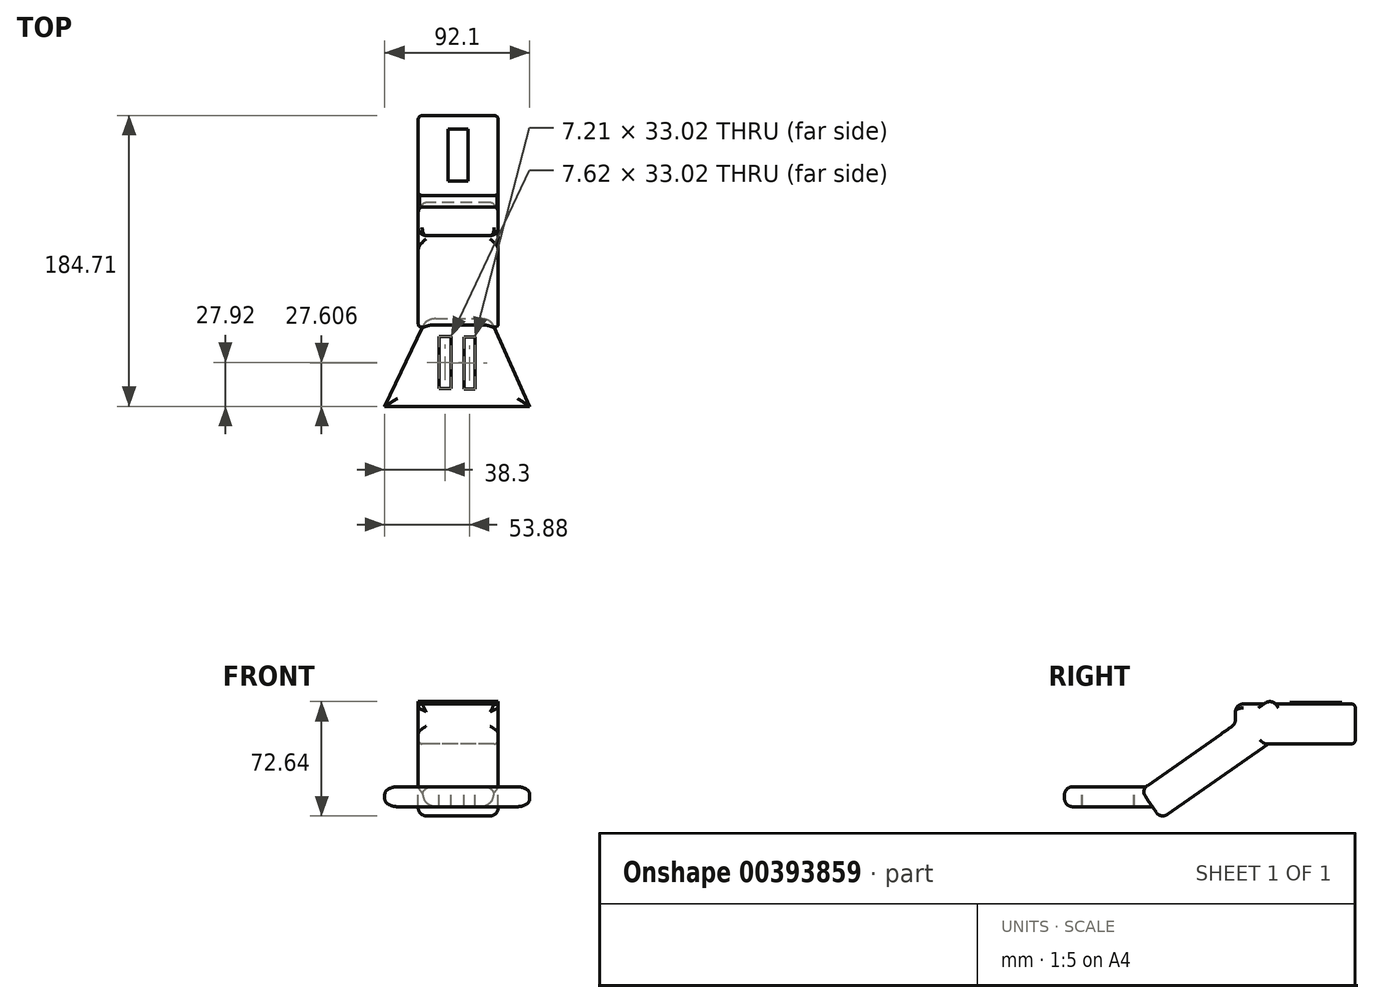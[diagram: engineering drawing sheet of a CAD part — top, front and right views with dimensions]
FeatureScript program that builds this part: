
annotation { "Feature Type Name" : "Feature", "Feature Type Description" : "" }
export const myFeature = defineFeature(function(context is Context, id is Id, definition is map)
    precondition{}
    {
        {
            var Q0;
            Q0=qCreatedBy(makeId("Front.planeOp"),FACE);
            var sketch = newSketch(context, id + "F0", { "sketchPlane" : qUnion([Q0])});
            skLineSegment(sketch, "E0.bottom", {"start": v(25.4, 12.7) * mm, "end": v(-25.4, 12.7) * mm});
            skLineSegment(sketch, "E0.top", {"start": v(25.4, -12.7) * mm, "end": v(-25.4, -12.7) * mm});
            skLineSegment(sketch, "E0.left", {"start": v(25.4, 12.7) * mm, "end": v(25.4, -12.7) * mm});
            skLineSegment(sketch, "E0.right", {"start": v(-25.4, 12.7) * mm, "end": v(-25.4, -12.7) * mm});
            skPoint(sketch, "E0.middle", {"position": v(0, 0) * mm});
            skSolve(sketch);
        }
        {
            var Q0;
            Q0=makeQuery(id+"F0.imprint","IMPRINT",FACE,{"disambiguationData":[TD([[makeQuery(id+"F0.imprint","IMPRINT",EDGE,{"derivedFrom":sQuery(id+"F0.wireOp",EDGE,"E0.bottom")}),1.0]])]});
            extrude(context, id + "F1", {"entities" : qUnion([Q0]), "oppositeDirection" : true, "depth" : 76.2 * mm});
        }
        {
            var Q0;
            Q0=makeQuery(id+"F1.opExtrude","SWEPT_EDGE",EDGE,{"disambiguationData":[OSD([sQuery(id+"F0.wireOp",EDGE,"E0.bottom"),sQuery(id+"F0.wireOp",EDGE,"E0.left")])]});
            var Q1;
            Q1=makeQuery(id+"F1.opExtrude","SWEPT_EDGE",EDGE,{"disambiguationData":[OSD([sQuery(id+"F0.wireOp",EDGE,"E0.bottom"),sQuery(id+"F0.wireOp",EDGE,"E0.right")])]});
            var Q2;
            Q2=makeQuery(id+"F1.opExtrude","SWEPT_EDGE",EDGE,{"disambiguationData":[OSD([sQuery(id+"F0.wireOp",EDGE,"E0.top"),sQuery(id+"F0.wireOp",EDGE,"E0.left")])]});
            var Q3;
            Q3=makeQuery(id+"F1.opExtrude","SWEPT_EDGE",EDGE,{"disambiguationData":[OSD([sQuery(id+"F0.wireOp",EDGE,"E0.top"),sQuery(id+"F0.wireOp",EDGE,"E0.right")])]});
            var Q4;
            Q4=makeQuery(id+"F1.opExtrude","CAP_EDGE",EDGE,{"disambiguationData":[OSD([sQuery(id+"F0.wireOp",EDGE,"E0.bottom")])],"isStart":false});
            var Q5;
            Q5=makeQuery(id+"F1.opExtrude","CAP_EDGE",EDGE,{"disambiguationData":[OSD([sQuery(id+"F0.wireOp",EDGE,"E0.right")])],"isStart":false});
            var Q6;
            Q6=makeQuery(id+"F1.opExtrude","CAP_EDGE",EDGE,{"disambiguationData":[OSD([sQuery(id+"F0.wireOp",EDGE,"E0.top")])],"isStart":false});
            var Q7;
            Q7=makeQuery(id+"F1.opExtrude","CAP_EDGE",EDGE,{"disambiguationData":[OSD([sQuery(id+"F0.wireOp",EDGE,"E0.left")])],"isStart":false});
            fillet(context, id + "F2", {"entities" : qUnion([Q0, Q1, Q2, Q3, Q4, Q5, Q6, Q7]), "radius" : 2.54 * mm, "tangentPropagation" : true, "allowEdgeOverflow" : false});
        }
        {
            var Q0;
            Q0=qCreatedBy(makeId("Front.planeOp"),FACE);
            cPlane(context, id + "F3", {"entities" : qUnion([Q0]), "cplaneType" : CPlaneType.OFFSET, "offset" : 50.8 * mm, "width" : 152.4 * mm, "height" : 152.4 * mm});
        }
        {
            var Q0;
            Q0=qCreatedBy(makeId("Top.planeOp"),FACE);
            var sketch = newSketch(context, id + "F4", { "sketchPlane" : qUnion([Q0])});
            skLineSegment(sketch, "E1", {"start": v(-76, 0) * mm, "end": v(75.54, 0) * mm, "construction": true});
            skSolve(sketch);
        }
        {
            var Q0;
            Q0=qCreatedBy(makeId("Top.planeOp"),FACE);
            var Q1;
            Q1=sQuery(id+"F4.wireOp",EDGE,"E1");
            cPlane(context, id + "F5", {"entities" : qUnion([Q0, Q1]), "cplaneType" : CPlaneType.LINE_ANGLE, "offset" : 25.4 * mm, "angle" : 35 * degree, "width" : 152.4 * mm, "height" : 152.4 * mm});
        }
        {
            var Q0;
            Q0=qCreatedBy(id+"F5.planeOp",FACE);
            var sketch = newSketch(context, id + "F6", { "sketchPlane" : qUnion([Q0])});
            skLineSegment(sketch, "E2.bottom", {"start": v(25.4, 73.45) * mm, "end": v(-25.4, 73.45) * mm});
            skLineSegment(sketch, "E2.top", {"start": v(25.4, -28.15) * mm, "end": v(-25.4, -28.15) * mm});
            skLineSegment(sketch, "E2.left", {"start": v(25.4, 73.45) * mm, "end": v(25.4, -28.15) * mm});
            skLineSegment(sketch, "E2.right", {"start": v(-25.4, 73.45) * mm, "end": v(-25.4, -28.15) * mm});
            skPoint(sketch, "E2.middle", {"position": v(0, 22.65) * mm});
            skSolve(sketch);
        }
        {
            var Q0;
            Q0=makeQuery(id+"F6.imprint","IMPRINT",FACE,{"disambiguationData":[TD([[makeQuery(id+"F6.imprint","IMPRINT",EDGE,{"derivedFrom":sQuery(id+"F6.wireOp",EDGE,"E2.bottom")}),1.0]])]});
            extrude(context, id + "F7", {"entities" : qUnion([Q0]), "operationType" : NewBodyOperationType.ADD, "depth" : 22.35 * mm});
        }
        {
            var Q0;
            Q0=makeQuery(id+"F7.opExtrude","CAP_EDGE",EDGE,{"disambiguationData":[OSD([sQuery(id+"F6.wireOp",EDGE,"E2.top")])],"isStart":true});
            var Q1;
            Q1=makeQuery(id+"F1.opExtrude","CAP_FACE",FACE,{"disambiguationData":[OSD([sQuery(id+"F0.wireOp",EDGE,"E0.bottom"),sQuery(id+"F0.wireOp",EDGE,"E0.top"),sQuery(id+"F0.wireOp",EDGE,"E0.left"),sQuery(id+"F0.wireOp",EDGE,"E0.right")])],"isStart":true});
            var Q2;
            Q2=makeQuery(id+"F7.opExtrude","CAP_EDGE",EDGE,{"disambiguationData":[OSD([sQuery(id+"F6.wireOp",EDGE,"E2.left")])],"isStart":false});
            var Q3;
            Q3=makeQuery(id+"F7.opExtrude","CAP_EDGE",EDGE,{"disambiguationData":[OSD([sQuery(id+"F6.wireOp",EDGE,"E2.right")])],"isStart":false});
            var Q4;
            Q4=makeQuery(id+"F7.opExtrude","CAP_EDGE",EDGE,{"disambiguationData":[OSD([sQuery(id+"F6.wireOp",EDGE,"E2.bottom")])],"isStart":false});
            var Q5;
            Q5=makeQuery(id+"F7.opExtrude","SWEPT_EDGE",EDGE,{"disambiguationData":[OSD([sQuery(id+"F6.wireOp",EDGE,"E2.bottom"),sQuery(id+"F6.wireOp",EDGE,"E2.left")])]});
            var Q6;
            Q6=makeQuery(id+"F7.opExtrude","CAP_EDGE",EDGE,{"disambiguationData":[OSD([sQuery(id+"F6.wireOp",EDGE,"E2.bottom")])],"isStart":true});
            var Q7;
            Q7=makeQuery(id+"F7.opExtrude","SWEPT_EDGE",EDGE,{"disambiguationData":[OSD([sQuery(id+"F6.wireOp",EDGE,"E2.bottom"),sQuery(id+"F6.wireOp",EDGE,"E2.right")])]});
            fillet(context, id + "F8", {"entities" : qUnion([Q0, Q1, Q2, Q3, Q4, Q5, Q6, Q7]), "radius" : 5.08 * mm, "tangentPropagation" : true, "allowEdgeOverflow" : false});
        }
        {
            var Q0;
            Q0=qCreatedBy(makeId("Top.planeOp"),FACE);
            cPlane(context, id + "F9", {"entities" : qUnion([Q0]), "cplaneType" : CPlaneType.OFFSET, "offset" : 52.58 * mm, "oppositeDirection" : true, "width" : 152.4 * mm, "height" : 152.4 * mm});
        }
        {
            var Q0;
            Q0=qCreatedBy(id+"F9.planeOp",FACE);
            var sketch = newSketch(context, id + "F10", { "sketchPlane" : qUnion([Q0])});
            skLineSegment(sketch, "E3", {"start": v(19.22, -50.68) * mm, "end": v(45.43, -108.51) * mm});
            skLineSegment(sketch, "E4", {"start": v(45.43, -108.51) * mm, "end": v(-46.67, -108.51) * mm});
            skLineSegment(sketch, "E5", {"start": v(-46.67, -108.51) * mm, "end": v(-19.27, -51.23) * mm});
            skLineSegment(sketch, "E6", {"start": v(-19.27, -51.23) * mm, "end": v(19.22, -50.68) * mm});
            skSolve(sketch);
        }
        {
            var Q0;
            Q0=makeQuery(id+"F10.imprint","IMPRINT",FACE,{"disambiguationData":[TD([[makeQuery(id+"F10.imprint","IMPRINT",EDGE,{"derivedFrom":sQuery(id+"F10.wireOp",EDGE,"E3")}),-1.0]])]});
            extrude(context, id + "F11", {"entities" : qUnion([Q0]), "operationType" : NewBodyOperationType.ADD, "depth" : 12.7 * mm});
        }
        {
            var Q0;
            Q0=makeQuery(id+"F11.opExtrude","CAP_EDGE",EDGE,{"disambiguationData":[OSD([sQuery(id+"F10.wireOp",EDGE,"E5")])],"isStart":false});
            var Q1;
            Q1=makeQuery(id+"F11.opExtrude","CAP_EDGE",EDGE,{"disambiguationData":[OSD([sQuery(id+"F10.wireOp",EDGE,"E3")])],"isStart":false});
            var Q2;
            Q2=makeQuery(id+"F11.opExtrude","CAP_EDGE",EDGE,{"disambiguationData":[OSD([sQuery(id+"F10.wireOp",EDGE,"E4")])],"isStart":false});
            var Q3;
            Q3=makeQuery(id+"F11.opExtrude","CAP_EDGE",EDGE,{"disambiguationData":[OSD([sQuery(id+"F10.wireOp",EDGE,"E4")])],"isStart":true});
            var Q4;
            Q4=makeQuery(id+"F11.opExtrude","CAP_EDGE",EDGE,{"disambiguationData":[OSD([sQuery(id+"F10.wireOp",EDGE,"E5")])],"isStart":true});
            var Q5;
            Q5=makeQuery(id+"F11.opExtrude","CAP_EDGE",EDGE,{"disambiguationData":[OSD([sQuery(id+"F10.wireOp",EDGE,"E3")])],"isStart":true});
            fillet(context, id + "F12", {"entities" : qUnion([Q0, Q1, Q2, Q3, Q4, Q5]), "radius" : 5.08 * mm, "tangentPropagation" : true, "allowEdgeOverflow" : false});
        }
        {
            var Q0;
            Q0=makeQuery(id+"F11.opExtrude","CAP_FACE",FACE,{"disambiguationData":[OSD([sQuery(id+"F10.wireOp",EDGE,"E3"),sQuery(id+"F10.wireOp",EDGE,"E4"),sQuery(id+"F10.wireOp",EDGE,"E5"),sQuery(id+"F10.wireOp",EDGE,"E6")])],"isStart":false});
            var sketch = newSketch(context, id + "F13", { "sketchPlane" : qUnion([Q0])});
            skLineSegment(sketch, "E7.bottom", {"start": v(-12.18, -64.08) * mm, "end": v(-4.56, -64.08) * mm});
            skLineSegment(sketch, "E7.top", {"start": v(-12.18, -97.1) * mm, "end": v(-4.56, -97.1) * mm});
            skLineSegment(sketch, "E7.left", {"start": v(-12.18, -64.08) * mm, "end": v(-12.18, -97.1) * mm});
            skLineSegment(sketch, "E7.right", {"start": v(-4.56, -64.08) * mm, "end": v(-4.56, -97.1) * mm});
            skSolve(sketch);
        }
        {
            var Q0;
            Q0=makeQuery(id+"F13.imprint","IMPRINT",FACE,{"disambiguationData":[TD([[makeQuery(id+"F13.imprint","IMPRINT",EDGE,{"derivedFrom":sQuery(id+"F13.wireOp",EDGE,"E7.bottom")}),1.0]])]});
            var sketch = newSketch(context, id + "F14", { "sketchPlane" : qUnion([Q0])});
            skLineSegment(sketch, "E8.bottom", {"start": v(3.6, -64.4) * mm, "end": v(10.81, -64.4) * mm});
            skLineSegment(sketch, "E8.top", {"start": v(3.6, -97.41) * mm, "end": v(10.81, -97.41) * mm});
            skLineSegment(sketch, "E8.left", {"start": v(3.6, -64.4) * mm, "end": v(3.6, -97.41) * mm});
            skLineSegment(sketch, "E8.right", {"start": v(10.81, -64.4) * mm, "end": v(10.81, -97.41) * mm});
            skSolve(sketch);
        }
        {
            var Q0;
            {var subQ1=sQuery(id+"F0.wireOp",EDGE,"E0.bottom");Q0=makeQuery(id+"F7.boolean.opBoolean","SPLIT",FACE,{"disambiguationData":[TD([makeQuery(id+"F2.opFillet","BLEND_FACE",FACE,{"disambiguationData":[OSD([subQ1])]})])],"derivedFrom":makeQuery(id+"F1.opExtrude","SWEPT_FACE",FACE,{"disambiguationData":[OSD([subQ1])]})});}
            var sketch = newSketch(context, id + "F15", { "sketchPlane" : qUnion([Q0])});
            skLineSegment(sketch, "E9.bottom", {"start": v(-6.4, 67.58) * mm, "end": v(6.3, 67.58) * mm});
            skLineSegment(sketch, "E9.top", {"start": v(-6.4, 34.56) * mm, "end": v(6.3, 34.56) * mm});
            skLineSegment(sketch, "E9.left", {"start": v(-6.4, 67.58) * mm, "end": v(-6.4, 34.56) * mm});
            skLineSegment(sketch, "E9.right", {"start": v(6.3, 67.58) * mm, "end": v(6.3, 34.56) * mm});
            skSolve(sketch);
        }
        {
            var Q0;
            Q0=makeQuery(id+"F13.imprint","IMPRINT",FACE,{"disambiguationData":[TD([[makeQuery(id+"F13.imprint","IMPRINT",EDGE,{"derivedFrom":sQuery(id+"F13.wireOp",EDGE,"E7.bottom")}),-1.0]])]});
            var Q1;
            Q1=makeQuery(id+"F14.imprint","IMPRINT",FACE,{"disambiguationData":[TD([[makeQuery(id+"F14.imprint","IMPRINT",EDGE,{"derivedFrom":sQuery(id+"F14.wireOp",EDGE,"E8.bottom")}),-1.0]])]});
            extrude(context, id + "F16", {"entities" : qUnion([Q0, Q1]), "operationType" : NewBodyOperationType.REMOVE, "oppositeDirection" : true, "depth" : 25.4 * mm});
        }
        {
            var Q0;
            Q0=makeQuery(id+"F15.imprint","IMPRINT",FACE,{"disambiguationData":[TD([[makeQuery(id+"F15.imprint","IMPRINT",EDGE,{"derivedFrom":sQuery(id+"F15.wireOp",EDGE,"E9.bottom")}),-1.0]])]});
            extrude(context, id + "F17", {"entities" : qUnion([Q0]), "operationType" : NewBodyOperationType.ADD, "depth" : 1.02 * mm});
        }
    });
